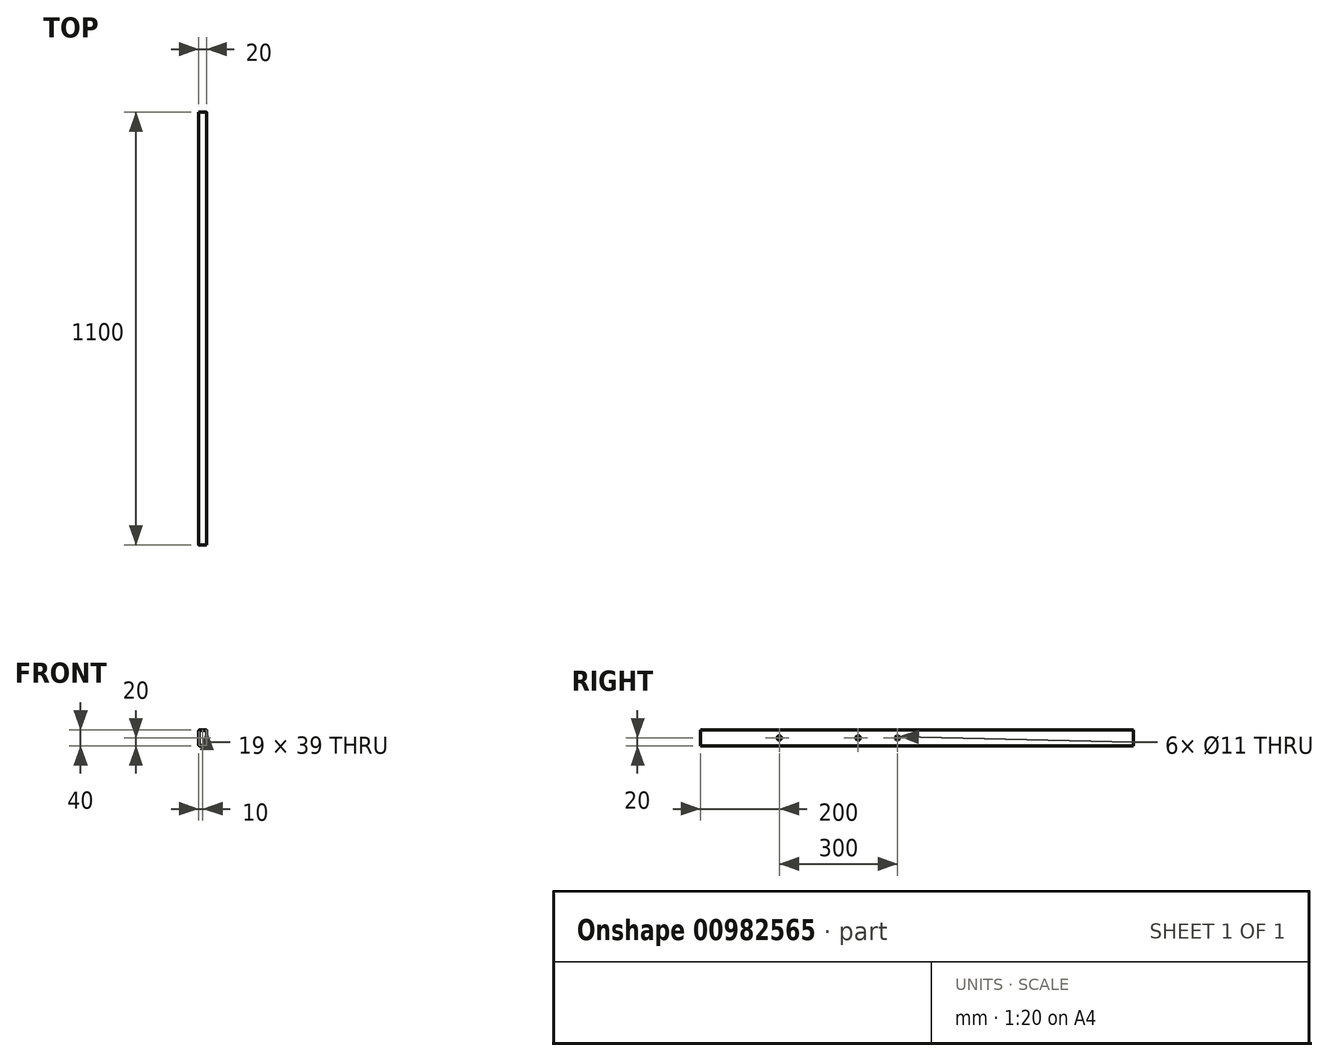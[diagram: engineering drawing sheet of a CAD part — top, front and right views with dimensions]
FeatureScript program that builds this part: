
annotation { "Feature Type Name" : "Feature", "Feature Type Description" : "" }
export const myFeature = defineFeature(function(context is Context, id is Id, definition is map)
    precondition{}
    {
        {
            var Q0;
            Q0=qCreatedBy(makeId("Front.planeOp"),FACE);
            var sketch = newSketch(context, id + "F0", { "sketchPlane" : qUnion([Q0])});
            skLineSegment(sketch, "E0.bottom", {"start": v(-9, 20) * mm, "end": v(9, 20) * mm});
            skLineSegment(sketch, "E0.top", {"start": v(-9, -20) * mm, "end": v(9, -20) * mm});
            skLineSegment(sketch, "E0.left", {"start": v(-10, 19) * mm, "end": v(-10, -19) * mm});
            skLineSegment(sketch, "E0.right", {"start": v(10, 19) * mm, "end": v(10, -19) * mm});
            skPoint(sketch, "E1.visualSharp", {"position": v(-10, 20) * mm});
            skArc(sketch, "E1.filletArc", {"start": v(-9, 20) * mm, "mid": v(-9.7, 19.7) * mm, "end": v(-10, 19) * mm});
            skPoint(sketch, "E2.visualSharp", {"position": v(10, 20) * mm});
            skArc(sketch, "E2.filletArc", {"start": v(10, 19) * mm, "mid": v(9.7, 19.7) * mm, "end": v(9, 20) * mm});
            skPoint(sketch, "E3.visualSharp", {"position": v(10, -20) * mm});
            skArc(sketch, "E3.filletArc", {"start": v(9, -20) * mm, "mid": v(9.7, -19.7) * mm, "end": v(10, -19) * mm});
            skPoint(sketch, "E4.visualSharp", {"position": v(-10, -20) * mm});
            skArc(sketch, "E4.filletArc", {"start": v(-10, -19) * mm, "mid": v(-9.7, -19.7) * mm, "end": v(-9, -20) * mm});
            skLineSegment(sketch, "E5.0", {"start": v(9.5, 19.5) * mm, "end": v(9.5, -19.5) * mm});
            skLineSegment(sketch, "E5.1", {"start": v(-9.5, 19.5) * mm, "end": v(9.5, 19.5) * mm});
            skLineSegment(sketch, "E5.2", {"start": v(-9.5, 19.5) * mm, "end": v(-9.5, -19.5) * mm});
            skLineSegment(sketch, "E5.3", {"start": v(-9.5, -19.5) * mm, "end": v(9.5, -19.5) * mm});
            skSolve(sketch);
        }
        {
            var Q0;
            Q0=makeQuery(id+"F0.imprint","IMPRINT",FACE,{"disambiguationData":[TD([[makeQuery(id+"F0.imprint","IMPRINT",EDGE,{"derivedFrom":sQuery(id+"F0.wireOp",EDGE,"f14a4ae3-e601-47cb-91da-211e3e1e951a.1.0.1")}),-1.0]])]});
            var Q1;
            Q1=makeQuery(id+"F0.imprint","IMPRINT",FACE,{"disambiguationData":[TD([[makeQuery(id+"F0.imprint","IMPRINT",EDGE,{"derivedFrom":sQuery(id+"F0.wireOp",EDGE,"f14a4ae3-e601-47cb-91da-211e3e1e951a.2.0.1")}),-1.0]])]});
            var Q2;
            Q2=makeQuery(id+"F0.imprint","IMPRINT",FACE,{"disambiguationData":[TD([[makeQuery(id+"F0.imprint","IMPRINT",EDGE,{"derivedFrom":sQuery(id+"F0.wireOp",EDGE,"52e9e63f-f607-447c-8eac-f1f637b628d7.1.3.0")}),-1.0]])]});
            var Q3;
            Q3=makeQuery(id+"F0.imprint","IMPRINT",FACE,{"disambiguationData":[TD([[makeQuery(id+"F0.imprint","IMPRINT",EDGE,{"derivedFrom":sQuery(id+"F0.wireOp",EDGE,"E0.bottom")}),-1.0]])]});
            extrude(context, id + "F1", {"entities" : qUnion([Q0, Q1, Q2, Q3]), "endBound" : BoundingType.SYMMETRIC, "depth" : 1100 * mm, "offsetDistance" : 25 * mm});
        }
        {
            var Q0;
            Q0=makeQuery(id+"F1.opExtrude","SWEPT_FACE",FACE,{"disambiguationData":[OSD([sQuery(id+"F0.wireOp",EDGE,"E0.right")])]});
            var sketch = newSketch(context, id + "F2", { "sketchPlane" : qUnion([Q0])});
            skPoint(sketch, "E6", {"position": v(-50, 0) * mm});
            skPoint(sketch, "E7", {"position": v(-150, 0) * mm});
            skPoint(sketch, "E8", {"position": v(-350, 0) * mm});
            skSolve(sketch);
        }
        {
            var Q0;
            Q0=sQuery(id+"F2.wireOp",VERTEX,"E6");
            var Q1;
            Q1=sQuery(id+"F2.wireOp",VERTEX,"E7");
            var Q2;
            Q2=sQuery(id+"F2.wireOp",VERTEX,"E8");
            var Q3;
            Q3=makeQuery(id+"F1.opExtrude","SWEPT_BODY",BODY,{"disambiguationData":[OSD([sQuery(id+"F0.wireOp",EDGE,"E0.bottom"),sQuery(id+"F0.wireOp",EDGE,"E0.top"),sQuery(id+"F0.wireOp",EDGE,"E0.left"),sQuery(id+"F0.wireOp",EDGE,"E0.right"),sQuery(id+"F0.wireOp",EDGE,"E1.filletArc"),sQuery(id+"F0.wireOp",EDGE,"E2.filletArc"),sQuery(id+"F0.wireOp",EDGE,"E3.filletArc"),sQuery(id+"F0.wireOp",EDGE,"E4.filletArc"),sQuery(id+"F0.wireOp",EDGE,"E5.0"),sQuery(id+"F0.wireOp",EDGE,"E5.1"),sQuery(id+"F0.wireOp",EDGE,"E5.2"),sQuery(id+"F0.wireOp",EDGE,"E5.3")])]});
            hole(context, id + "F3", {"style" : HoleStyle.SIMPLE, "endStyle" : HoleEndStyle.BLIND, "holeDiameter" : 11 * mm, "majorDiameter" : 5 * mm, "holeDepth" : 30 * mm, "isTappedThrough" : true, "tappedDepth" : 4 * mm, "tapClearance" : 3, "startFromSketch" : true, "locations" : qUnion([Q0, Q1, Q2]), "scope" : qUnion([Q3])});
        }
    });
